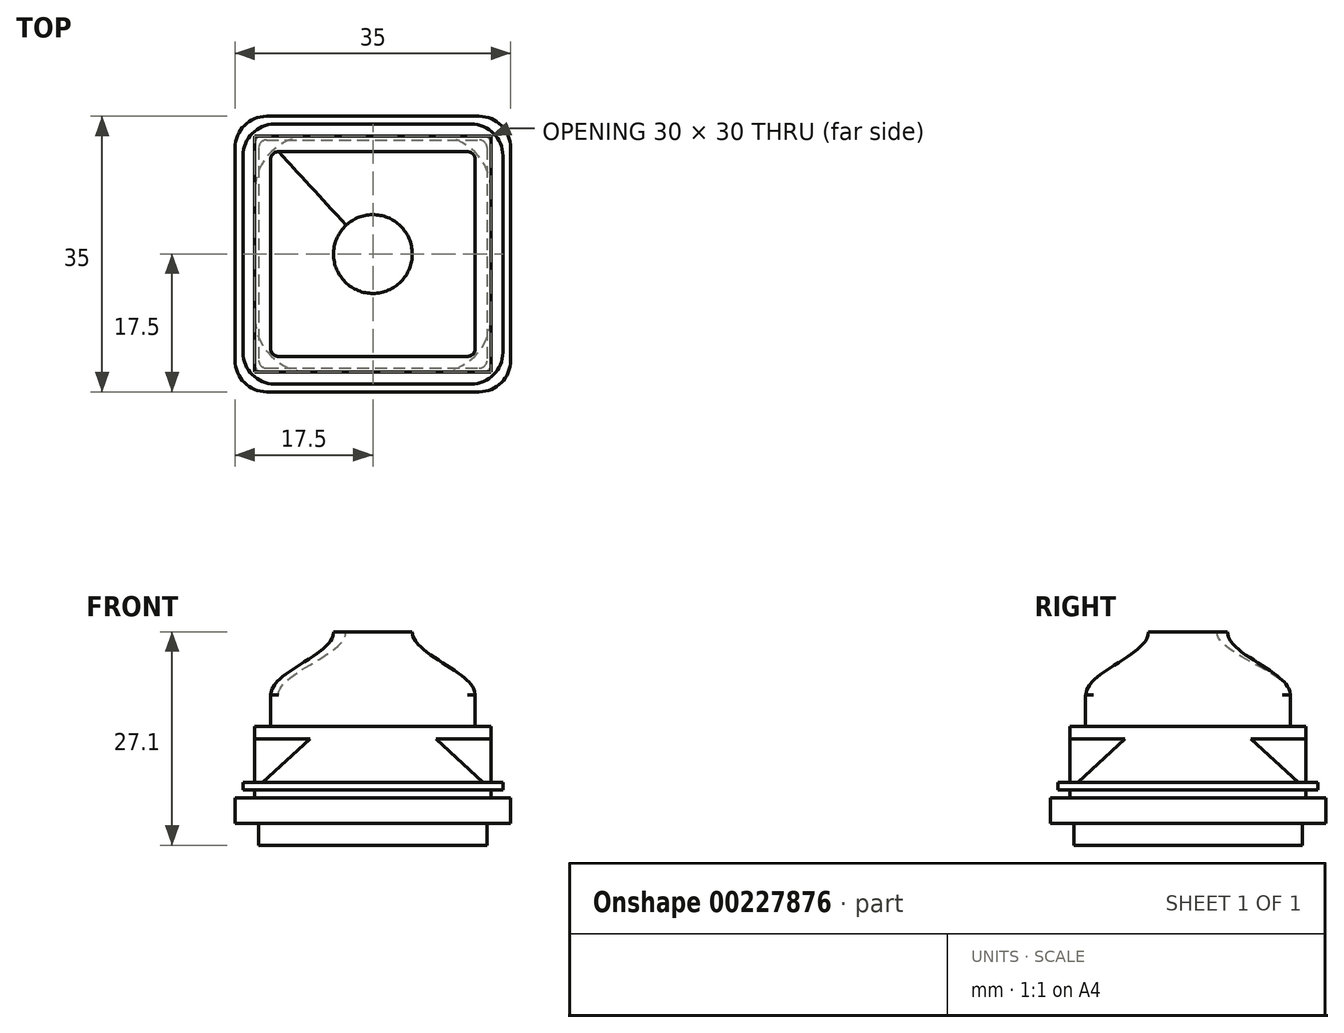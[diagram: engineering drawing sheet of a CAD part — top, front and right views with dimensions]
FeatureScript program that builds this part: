
annotation { "Feature Type Name" : "Feature", "Feature Type Description" : "" }
export const myFeature = defineFeature(function(context is Context, id is Id, definition is map)
    precondition{}
    {
        {
            var Q0;
            Q0=qCreatedBy(makeId("Top.planeOp"),FACE);
            var sketch = newSketch(context, id + "F0", { "sketchPlane" : qUnion([Q0])});
            skPoint(sketch, "E0.middle", {"position": v(0, 0) * mm});
            skLineSegment(sketch, "E1.bottom", {"start": v(-13.5, 14.5) * mm, "end": v(13.5, 14.5) * mm});
            skLineSegment(sketch, "E1.top", {"start": v(-13.5, -14.5) * mm, "end": v(13.5, -14.5) * mm});
            skLineSegment(sketch, "E1.left", {"start": v(-14.5, 13.5) * mm, "end": v(-14.5, -13.5) * mm});
            skLineSegment(sketch, "E1.right", {"start": v(14.5, 13.5) * mm, "end": v(14.5, -13.5) * mm});
            skPoint(sketch, "E2.visualSharp", {"position": v(14.5, 14.5) * mm});
            skArc(sketch, "E2.filletArc", {"start": v(14.5, 13.5) * mm, "mid": v(14.2, 14.2) * mm, "end": v(13.5, 14.5) * mm});
            skPoint(sketch, "E3.visualSharp", {"position": v(14.5, -14.5) * mm});
            skArc(sketch, "E3.filletArc", {"start": v(13.5, -14.5) * mm, "mid": v(14.2, -14.2) * mm, "end": v(14.5, -13.5) * mm});
            skPoint(sketch, "E4.visualSharp", {"position": v(-14.5, -14.5) * mm});
            skArc(sketch, "E4.filletArc", {"start": v(-14.5, -13.5) * mm, "mid": v(-14.2, -14.2) * mm, "end": v(-13.5, -14.5) * mm});
            skPoint(sketch, "E5.visualSharp", {"position": v(-14.5, 14.5) * mm});
            skArc(sketch, "E5.filletArc", {"start": v(-13.5, 14.5) * mm, "mid": v(-14.2, 14.2) * mm, "end": v(-14.5, 13.5) * mm});
            skSolve(sketch);
        }
        {
            var Q0;
            Q0=qCreatedBy(makeId("Top.planeOp"),FACE);
            cPlane(context, id + "F1", {"entities" : qUnion([Q0]), "cplaneType" : CPlaneType.OFFSET, "offset" : 2.8 * mm, "width" : 150 * mm, "height" : 150 * mm});
        }
        {
            var Q0;
            Q0=qCreatedBy(id+"F1.planeOp",FACE);
            var sketch = newSketch(context, id + "F2", { "sketchPlane" : qUnion([Q0])});
            skLineSegment(sketch, "E6.bottom", {"start": v(-13.5, 17.5) * mm, "end": v(13.5, 17.5) * mm});
            skLineSegment(sketch, "E6.top", {"start": v(-13.5, -17.5) * mm, "end": v(13.5, -17.5) * mm});
            skLineSegment(sketch, "E6.left", {"start": v(-17.5, 13.5) * mm, "end": v(-17.5, -13.5) * mm});
            skLineSegment(sketch, "E6.right", {"start": v(17.5, 13.5) * mm, "end": v(17.5, -13.5) * mm});
            skPoint(sketch, "E6.middle", {"position": v(0, 0) * mm});
            skPoint(sketch, "E7.visualSharp", {"position": v(-17.5, 17.5) * mm});
            skArc(sketch, "E7.filletArc", {"start": v(-13.5, 17.5) * mm, "mid": v(-16.33, 16.33) * mm, "end": v(-17.5, 13.5) * mm});
            skPoint(sketch, "E8.visualSharp", {"position": v(17.5, 17.5) * mm});
            skArc(sketch, "E8.filletArc", {"start": v(17.5, 13.5) * mm, "mid": v(16.33, 16.33) * mm, "end": v(13.5, 17.5) * mm});
            skPoint(sketch, "E9.visualSharp", {"position": v(17.5, -17.5) * mm});
            skArc(sketch, "E9.filletArc", {"start": v(13.5, -17.5) * mm, "mid": v(16.33, -16.33) * mm, "end": v(17.5, -13.5) * mm});
            skArc(sketch, "E10.filletArc", {"start": v(-17.5, -13.5) * mm, "mid": v(-16.33, -16.33) * mm, "end": v(-13.5, -17.5) * mm});
            skSolve(sketch);
        }
        {
            var Q0;
            Q0=qCreatedBy(id+"F1.planeOp",FACE);
            cPlane(context, id + "F3", {"entities" : qUnion([Q0]), "cplaneType" : CPlaneType.OFFSET, "offset" : 3.2 * mm, "width" : 150 * mm, "height" : 150 * mm});
        }
        {
            var Q0;
            Q0=qCreatedBy(id+"F3.planeOp",FACE);
            var sketch = newSketch(context, id + "F4", { "sketchPlane" : qUnion([Q0])});
            skPoint(sketch, "E11.middle", {"position": v(0, 0) * mm});
            skLineSegment(sketch, "E12.bottom", {"start": v(-14, 15) * mm, "end": v(14, 15) * mm});
            skLineSegment(sketch, "E12.top", {"start": v(-14, -15) * mm, "end": v(14, -15) * mm});
            skLineSegment(sketch, "E12.left", {"start": v(-15, 14) * mm, "end": v(-15, -14) * mm});
            skLineSegment(sketch, "E12.right", {"start": v(15, 14) * mm, "end": v(15, -14) * mm});
            skPoint(sketch, "E13.visualSharp", {"position": v(15, 15) * mm});
            skArc(sketch, "E13.filletArc", {"start": v(15, 14) * mm, "mid": v(14.7, 14.7) * mm, "end": v(14, 15) * mm});
            skPoint(sketch, "E14.visualSharp", {"position": v(15, -15) * mm});
            skArc(sketch, "E14.filletArc", {"start": v(14, -15) * mm, "mid": v(14.7, -14.7) * mm, "end": v(15, -14) * mm});
            skPoint(sketch, "E15.visualSharp", {"position": v(-15, -15) * mm});
            skArc(sketch, "E15.filletArc", {"start": v(-15, -14) * mm, "mid": v(-14.7, -14.7) * mm, "end": v(-14, -15) * mm});
            skPoint(sketch, "E16.visualSharp", {"position": v(-15, 15) * mm});
            skArc(sketch, "E16.filletArc", {"start": v(-14, 15) * mm, "mid": v(-14.7, 14.7) * mm, "end": v(-15, 14) * mm});
            skSolve(sketch);
        }
        {
            var Q0;
            Q0=qCreatedBy(id+"F3.planeOp",FACE);
            cPlane(context, id + "F5", {"entities" : qUnion([Q0]), "cplaneType" : CPlaneType.OFFSET, "offset" : 1 * mm, "width" : 150 * mm, "height" : 150 * mm});
        }
        {
            var Q0;
            Q0=qCreatedBy(id+"F5.planeOp",FACE);
            var sketch = newSketch(context, id + "F6", { "sketchPlane" : qUnion([Q0])});
            skLineSegment(sketch, "E17.bottom", {"start": v(-12.5, 16.5) * mm, "end": v(12.5, 16.5) * mm});
            skLineSegment(sketch, "E17.top", {"start": v(-12.5, -16.5) * mm, "end": v(12.5, -16.5) * mm});
            skLineSegment(sketch, "E17.left", {"start": v(-16.5, 12.5) * mm, "end": v(-16.5, -12.5) * mm});
            skLineSegment(sketch, "E17.right", {"start": v(16.5, 12.5) * mm, "end": v(16.5, -12.5) * mm});
            skPoint(sketch, "E17.middle", {"position": v(0, 0) * mm});
            skPoint(sketch, "E18.visualSharp", {"position": v(-16.5, 16.5) * mm});
            skArc(sketch, "E18.filletArc", {"start": v(-12.5, 16.5) * mm, "mid": v(-15.33, 15.33) * mm, "end": v(-16.5, 12.5) * mm});
            skPoint(sketch, "E19.visualSharp", {"position": v(16.5, 16.5) * mm});
            skArc(sketch, "E19.filletArc", {"start": v(16.5, 12.5) * mm, "mid": v(15.33, 15.33) * mm, "end": v(12.5, 16.5) * mm});
            skPoint(sketch, "E20.visualSharp", {"position": v(16.5, -16.5) * mm});
            skArc(sketch, "E20.filletArc", {"start": v(12.5, -16.5) * mm, "mid": v(15.33, -15.33) * mm, "end": v(16.5, -12.5) * mm});
            skArc(sketch, "E21.filletArc", {"start": v(-16.5, -12.5) * mm, "mid": v(-15.33, -15.33) * mm, "end": v(-12.5, -16.5) * mm});
            skSolve(sketch);
        }
        {
            var Q0;
            Q0=qCreatedBy(id+"F5.planeOp",FACE);
            cPlane(context, id + "F7", {"entities" : qUnion([Q0]), "cplaneType" : CPlaneType.OFFSET, "offset" : 1 * mm, "width" : 150 * mm, "height" : 150 * mm});
        }
        {
            var Q0;
            Q0=qCreatedBy(id+"F7.planeOp",FACE);
            var sketch = newSketch(context, id + "F8", { "sketchPlane" : qUnion([Q0])});
            skPoint(sketch, "E22.middle", {"position": v(0, 0) * mm});
            skLineSegment(sketch, "E23.bottom", {"start": v(-14, 15) * mm, "end": v(14, 15) * mm});
            skLineSegment(sketch, "E23.top", {"start": v(-14, -15) * mm, "end": v(14, -15) * mm});
            skLineSegment(sketch, "E23.left", {"start": v(-15, 14) * mm, "end": v(-15, -14) * mm});
            skLineSegment(sketch, "E23.right", {"start": v(15, 14) * mm, "end": v(15, -14) * mm});
            skPoint(sketch, "E24.visualSharp", {"position": v(15, 15) * mm});
            skArc(sketch, "E24.filletArc", {"start": v(15, 14) * mm, "mid": v(14.7, 14.7) * mm, "end": v(14, 15) * mm});
            skPoint(sketch, "E25.visualSharp", {"position": v(15, -15) * mm});
            skArc(sketch, "E25.filletArc", {"start": v(14, -15) * mm, "mid": v(14.7, -14.7) * mm, "end": v(15, -14) * mm});
            skPoint(sketch, "E26.visualSharp", {"position": v(-15, -15) * mm});
            skArc(sketch, "E26.filletArc", {"start": v(-15, -14) * mm, "mid": v(-14.7, -14.7) * mm, "end": v(-14, -15) * mm});
            skPoint(sketch, "E27.visualSharp", {"position": v(-15, 15) * mm});
            skArc(sketch, "E27.filletArc", {"start": v(-14, 15) * mm, "mid": v(-14.7, 14.7) * mm, "end": v(-15, 14) * mm});
            skSolve(sketch);
        }
        {
            var Q0;
            Q0=qCreatedBy(id+"F7.planeOp",FACE);
            cPlane(context, id + "F9", {"entities" : qUnion([Q0]), "cplaneType" : CPlaneType.OFFSET, "offset" : 5.5 * mm, "width" : 150 * mm, "height" : 150 * mm});
        }
        {
            var Q0;
            Q0=qCreatedBy(id+"F9.planeOp",FACE);
            var sketch = newSketch(context, id + "F10", { "sketchPlane" : qUnion([Q0])});
            skPoint(sketch, "E28.middle", {"position": v(0, 0) * mm});
            skLineSegment(sketch, "E29.bottom", {"start": v(-8, 15) * mm, "end": v(8, 15) * mm});
            skLineSegment(sketch, "E29.top", {"start": v(-8, -15) * mm, "end": v(8, -15) * mm});
            skLineSegment(sketch, "E29.left", {"start": v(-15, 8) * mm, "end": v(-15, -8) * mm});
            skLineSegment(sketch, "E29.right", {"start": v(15, 8) * mm, "end": v(15, -8) * mm});
            skPoint(sketch, "E30.visualSharp", {"position": v(15, 15) * mm});
            skArc(sketch, "E30.filletArc", {"start": v(15, 8) * mm, "mid": v(12.95, 12.95) * mm, "end": v(8, 15) * mm});
            skPoint(sketch, "E31.visualSharp", {"position": v(15, -15) * mm});
            skArc(sketch, "E31.filletArc", {"start": v(8, -15) * mm, "mid": v(12.95, -12.95) * mm, "end": v(15, -8) * mm});
            skPoint(sketch, "E32.visualSharp", {"position": v(-15, -15) * mm});
            skArc(sketch, "E32.filletArc", {"start": v(-15, -8) * mm, "mid": v(-12.95, -12.95) * mm, "end": v(-8, -15) * mm});
            skPoint(sketch, "E33.visualSharp", {"position": v(-15, 15) * mm});
            skArc(sketch, "E33.filletArc", {"start": v(-8, 15) * mm, "mid": v(-12.95, 12.95) * mm, "end": v(-15, 8) * mm});
            skLineSegment(sketch, "E34.bottom", {"start": v(-15, 15) * mm, "end": v(15, 15) * mm});
            skLineSegment(sketch, "E34.top", {"start": v(-15, -15) * mm, "end": v(15, -15) * mm});
            skLineSegment(sketch, "E34.left", {"start": v(-15, 15) * mm, "end": v(-15, -15) * mm});
            skLineSegment(sketch, "E34.right", {"start": v(15, 15) * mm, "end": v(15, -15) * mm});
            skLineSegment(sketch, "E35.filletArc", {"start": v(-15, 15) * mm, "end": v(-15, 15) * mm});
            skLineSegment(sketch, "E36.filletArc", {"start": v(15, 15) * mm, "end": v(15, 15) * mm});
            skLineSegment(sketch, "E37.filletArc", {"start": v(15, -15) * mm, "end": v(15, -15) * mm});
            skLineSegment(sketch, "E38.filletArc", {"start": v(-15, -15) * mm, "end": v(-15, -15) * mm});
            skSolve(sketch);
        }
        {
            var Q0;
            Q0=qCreatedBy(id+"F9.planeOp",FACE);
            cPlane(context, id + "F11", {"entities" : qUnion([Q0]), "cplaneType" : CPlaneType.OFFSET, "offset" : 1.6 * mm, "width" : 150 * mm, "height" : 150 * mm});
        }
        {
            var Q0;
            Q0=qCreatedBy(id+"F11.planeOp",FACE);
            var sketch = newSketch(context, id + "F12", { "sketchPlane" : qUnion([Q0])});
            skPoint(sketch, "E39.middle", {"position": v(0, 0) * mm});
            skLineSegment(sketch, "E40.bottom", {"start": v(-12, 13) * mm, "end": v(12, 13) * mm});
            skLineSegment(sketch, "E40.top", {"start": v(-12, -13) * mm, "end": v(12, -13) * mm});
            skLineSegment(sketch, "E40.left", {"start": v(-13, 12) * mm, "end": v(-13, -12) * mm});
            skLineSegment(sketch, "E40.right", {"start": v(13, 12) * mm, "end": v(13, -12) * mm});
            skPoint(sketch, "E41.visualSharp", {"position": v(13, 13) * mm});
            skArc(sketch, "E41.filletArc", {"start": v(13, 12) * mm, "mid": v(12.7, 12.7) * mm, "end": v(12, 13) * mm});
            skPoint(sketch, "E42.visualSharp", {"position": v(13, -13) * mm});
            skArc(sketch, "E42.filletArc", {"start": v(12, -13) * mm, "mid": v(12.7, -12.7) * mm, "end": v(13, -12) * mm});
            skPoint(sketch, "E43.visualSharp", {"position": v(-13, -13) * mm});
            skArc(sketch, "E43.filletArc", {"start": v(-13, -12) * mm, "mid": v(-12.7, -12.7) * mm, "end": v(-12, -13) * mm});
            skPoint(sketch, "E44.visualSharp", {"position": v(-13, 13) * mm});
            skArc(sketch, "E44.filletArc", {"start": v(-12, 13) * mm, "mid": v(-12.7, 12.7) * mm, "end": v(-13, 12) * mm});
            skSolve(sketch);
        }
        {
            var Q0;
            Q0=qCreatedBy(id+"F11.planeOp",FACE);
            cPlane(context, id + "F13", {"entities" : qUnion([Q0]), "cplaneType" : CPlaneType.OFFSET, "offset" : 4 * mm, "width" : 150 * mm, "height" : 150 * mm});
        }
        {
            var Q0;
            Q0=qCreatedBy(id+"F13.planeOp",FACE);
            var sketch = newSketch(context, id + "F14", { "sketchPlane" : qUnion([Q0])});
            skPoint(sketch, "E45.middle", {"position": v(0, 0) * mm});
            skLineSegment(sketch, "E46.bottom", {"start": v(-12, 13) * mm, "end": v(12, 13) * mm});
            skLineSegment(sketch, "E46.top", {"start": v(-12, -13) * mm, "end": v(12, -13) * mm});
            skLineSegment(sketch, "E46.left", {"start": v(-13, 12) * mm, "end": v(-13, -12) * mm});
            skLineSegment(sketch, "E46.right", {"start": v(13, 12) * mm, "end": v(13, -12) * mm});
            skPoint(sketch, "E47.visualSharp", {"position": v(13, 13) * mm});
            skArc(sketch, "E47.filletArc", {"start": v(13, 12) * mm, "mid": v(12.7, 12.7) * mm, "end": v(12, 13) * mm});
            skPoint(sketch, "E48.visualSharp", {"position": v(13, -13) * mm});
            skArc(sketch, "E48.filletArc", {"start": v(12, -13) * mm, "mid": v(12.7, -12.7) * mm, "end": v(13, -12) * mm});
            skPoint(sketch, "E49.visualSharp", {"position": v(-13, -13) * mm});
            skArc(sketch, "E49.filletArc", {"start": v(-13, -12) * mm, "mid": v(-12.7, -12.7) * mm, "end": v(-12, -13) * mm});
            skPoint(sketch, "E50.visualSharp", {"position": v(-13, 13) * mm});
            skArc(sketch, "E50.filletArc", {"start": v(-12, 13) * mm, "mid": v(-12.7, 12.7) * mm, "end": v(-13, 12) * mm});
            skSolve(sketch);
        }
        {
            var Q0;
            Q0=qCreatedBy(id+"F13.planeOp",FACE);
            cPlane(context, id + "F15", {"entities" : qUnion([Q0]), "cplaneType" : CPlaneType.OFFSET, "offset" : 8 * mm, "width" : 150 * mm, "height" : 150 * mm});
        }
        {
            var Q0;
            Q0=qCreatedBy(id+"F15.planeOp",FACE);
            var sketch = newSketch(context, id + "F16", { "sketchPlane" : qUnion([Q0])});
            skCircle(sketch, "E51", {"center": v(0, 0) * mm, "radius": 5 * mm});
            skSolve(sketch);
        }
        {
            var Q0;
            Q0=makeQuery(id+"F14.imprint","IMPRINT",FACE,{"disambiguationData":[TD([[makeQuery(id+"F14.imprint","IMPRINT",EDGE,{"derivedFrom":sQuery(id+"F14.wireOp",EDGE,"E46.bottom")}),-1.0]])]});
            var Q1;
            Q1=makeQuery(id+"F16.imprint","IMPRINT",FACE,{"disambiguationData":[TD([[makeQuery(id+"F16.imprint","IMPRINT",EDGE,{"derivedFrom":sQuery(id+"F16.wireOp",EDGE,"E51")}),1.0]])]});
            loft(context, id + "F17", {"startCondition" : LoftEndDerivativeType.NORMAL_TO_PROFILE, "startMagnitude" : 1, "endCondition" : LoftEndDerivativeType.NORMAL_TO_PROFILE, "endMagnitude" : 1, "sheetProfilesArray" : [{ "sheetProfileEntities" : qUnion([Q0]) }, { "sheetProfileEntities" : qUnion([Q1]) }]});
        }
        {
            var Q0;
            Q0=qSketchRegion(id+"F12",true);
            extrude(context, id + "F18", {"entities" : qUnion([Q0]), "operationType" : NewBodyOperationType.ADD, "endBound" : BoundingType.UP_TO_NEXT, "depth" : 25 * mm});
        }
        {
            var Q0;
            Q0=qSketchRegion(id+"F10",true);
            var Q1;
            Q1=makeQuery(id+"F10.imprint","IMPRINT",FACE,{"disambiguationData":[TD([[makeQuery(id+"F10.imprint","IMPRINT",EDGE,{"derivedFrom":sQuery(id+"F10.wireOp",EDGE,"E29.bottom")}),-1.0]])]});
            var Q2;
            Q2=makeQuery(id+"F18.opExtrude","CAP_FACE",FACE,{"disambiguationData":[OSD([sQuery(id+"F12.wireOp",EDGE,"E40.bottom"),sQuery(id+"F12.wireOp",EDGE,"E40.top"),sQuery(id+"F12.wireOp",EDGE,"E40.left"),sQuery(id+"F12.wireOp",EDGE,"E40.right"),sQuery(id+"F12.wireOp",EDGE,"E41.filletArc"),sQuery(id+"F12.wireOp",EDGE,"E42.filletArc"),sQuery(id+"F12.wireOp",EDGE,"E43.filletArc"),sQuery(id+"F12.wireOp",EDGE,"E44.filletArc")])],"isStart":true});
            extrude(context, id + "F19", {"entities" : qUnion([Q0, Q1]), "operationType" : NewBodyOperationType.ADD, "endBound" : BoundingType.UP_TO_SURFACE, "endBoundEntityFace" : qUnion([Q2]), "depth" : 25 * mm});
        }
        {
            var Q0;
            {var subQ3=sQuery(id+"F10.wireOp",EDGE,"E30.filletArc");Q0=makeQuery(id+"F10.imprint","IMPRINT",FACE,{"disambiguationData":[TD([[makeQuery(id+"F10.imprint","IMPRINT",EDGE,{"derivedFrom":subQ3}),1.0]])]});}
            var Q1;
            Q1=makeQuery(id+"F8.imprint","IMPRINT",FACE,{"disambiguationData":[TD([[makeQuery(id+"F8.imprint","IMPRINT",EDGE,{"derivedFrom":sQuery(id+"F8.wireOp",EDGE,"E23.bottom")}),-1.0]])]});
            loft(context, id + "F20", {"operationType" : NewBodyOperationType.ADD, "sheetProfilesArray" : [{ "sheetProfileEntities" : qUnion([Q0]) }, { "sheetProfileEntities" : qUnion([Q1]) }]});
        }
        {
            var Q0;
            Q0=makeQuery(id+"F6.imprint","IMPRINT",FACE,{"disambiguationData":[TD([[makeQuery(id+"F6.imprint","IMPRINT",EDGE,{"derivedFrom":sQuery(id+"F6.wireOp",EDGE,"E17.bottom")}),-1.0]])]});
            var Q1;
            Q1=makeQuery(id+"F20.opLoft","CAP_FACE",FACE,{"disambiguationData":[OSD([makeQuery(id+"F8.imprint","IMPRINT",FACE,{"disambiguationData":[TD([[makeQuery(id+"F8.imprint","IMPRINT",EDGE,{"derivedFrom":sQuery(id+"F8.wireOp",EDGE,"E23.bottom")}),-1.0]])]})])],"isStart":true});
            extrude(context, id + "F21", {"entities" : qUnion([Q0]), "operationType" : NewBodyOperationType.ADD, "endBound" : BoundingType.UP_TO_SURFACE, "endBoundEntityFace" : qUnion([Q1]), "depth" : 25 * mm});
        }
        {
            var Q0;
            Q0=makeQuery(id+"F4.imprint","IMPRINT",FACE,{"disambiguationData":[TD([[makeQuery(id+"F4.imprint","IMPRINT",EDGE,{"derivedFrom":sQuery(id+"F4.wireOp",EDGE,"E12.bottom")}),-1.0]])]});
            extrude(context, id + "F22", {"entities" : qUnion([Q0]), "operationType" : NewBodyOperationType.ADD, "endBound" : BoundingType.UP_TO_NEXT, "depth" : 25 * mm});
        }
        {
            var Q0;
            Q0=makeQuery(id+"F2.imprint","IMPRINT",FACE,{"disambiguationData":[TD([[makeQuery(id+"F2.imprint","IMPRINT",EDGE,{"derivedFrom":sQuery(id+"F2.wireOp",EDGE,"E6.bottom")}),-1.0]])]});
            var Q1;
            Q1=makeQuery(id+"F22.opExtrude","CAP_FACE",FACE,{"disambiguationData":[OSD([sQuery(id+"F4.wireOp",EDGE,"E12.bottom"),sQuery(id+"F4.wireOp",EDGE,"E12.top"),sQuery(id+"F4.wireOp",EDGE,"E12.left"),sQuery(id+"F4.wireOp",EDGE,"E12.right"),sQuery(id+"F4.wireOp",EDGE,"E13.filletArc"),sQuery(id+"F4.wireOp",EDGE,"E14.filletArc"),sQuery(id+"F4.wireOp",EDGE,"E15.filletArc"),sQuery(id+"F4.wireOp",EDGE,"E16.filletArc")])],"isStart":true});
            var Q2;
            Q2=makeQuery(id+"F17.opLoft","SWEPT_BODY",BODY,{"disambiguationData":[OSD([makeQuery(id+"F14.imprint","IMPRINT",FACE,{"disambiguationData":[TD([[makeQuery(id+"F14.imprint","IMPRINT",EDGE,{"derivedFrom":sQuery(id+"F14.wireOp",EDGE,"E46.bottom")}),-1.0]])]}),makeQuery(id+"F16.imprint","IMPRINT",FACE,{"disambiguationData":[TD([[makeQuery(id+"F16.imprint","IMPRINT",EDGE,{"derivedFrom":sQuery(id+"F16.wireOp",EDGE,"E51")}),1.0]])]})])]});
            extrude(context, id + "F23", {"entities" : qUnion([Q0]), "operationType" : NewBodyOperationType.ADD, "endBound" : BoundingType.UP_TO_SURFACE, "endBoundEntityFace" : qUnion([Q1]), "endBoundEntityBody" : qUnion([Q2]), "depth" : 25 * mm});
        }
        {
            var Q0;
            Q0=makeQuery(id+"F0.imprint","IMPRINT",FACE,{"disambiguationData":[TD([[makeQuery(id+"F0.imprint","IMPRINT",EDGE,{"derivedFrom":sQuery(id+"F0.wireOp",EDGE,"E1.bottom")}),-1.0]])]});
            var Q1;
            Q1=makeQuery(id+"F23.opExtrude","CAP_FACE",FACE,{"disambiguationData":[OSD([sQuery(id+"F2.wireOp",EDGE,"E6.bottom"),sQuery(id+"F2.wireOp",EDGE,"E6.top"),sQuery(id+"F2.wireOp",EDGE,"E6.left"),sQuery(id+"F2.wireOp",EDGE,"E6.right"),sQuery(id+"F2.wireOp",EDGE,"E7.filletArc"),sQuery(id+"F2.wireOp",EDGE,"E8.filletArc"),sQuery(id+"F2.wireOp",EDGE,"E9.filletArc"),sQuery(id+"F2.wireOp",EDGE,"E10.filletArc")])],"isStart":true});
            extrude(context, id + "F24", {"entities" : qUnion([Q0]), "operationType" : NewBodyOperationType.ADD, "endBound" : BoundingType.UP_TO_SURFACE, "endBoundEntityFace" : qUnion([Q1]), "depth" : 25 * mm});
        }
    });
